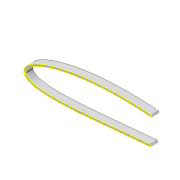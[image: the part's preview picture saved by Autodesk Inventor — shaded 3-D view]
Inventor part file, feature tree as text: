
AUTODESK INVENTOR PART (.ipt)
format: ipt  version: 2022 (Build 260153000, 153)  size: 441,344 bytes
history: native  units: mm
features: sketch x4, extrude x2, thicken_offset x2, shell x1, other x1, projected_geometry x1
ambient origin geometry x8: Origin, YZ Plane, XZ Plane, XY Plane, X Axis, Y Axis, Z Axis, Center Point
bodies: Solid1 (feature_tree)
feature tree (11):
  extrude  "Extrusion1"  Depth=3.0mm
  shell  "Shell1"  Thickness=1.0mm
  thicken_offset  "Thicken1"
  extrude  "Extrusion27"  TaperAngle=0.0deg  [1 undecoded]
  other  "Bend Part1"
  thicken_offset  "Thicken2"
  sketch  "Sketch52"  dims[d247=1.0mm d248=1.0mm]
  sketch  "Sketch3"  dims[d0=10.0mm d1=0.0mm d2=3.0mm d159=1.0mm d160=2.0mm]
  sketch  "Sketch48"  dims[d236=190.0mm d237=0.0mm d238=0.0mm]
  sketch  "Sketch49"  dims[d239=10.0mm d240=0.872665mm]
  projected_geometry  "Project Cut Edges3"
note: 1 required parameter value undecoded (feature->parameter linkage not recoverable at this tier; creation-order binding heuristic only, values carry confidence <= 0.55)
